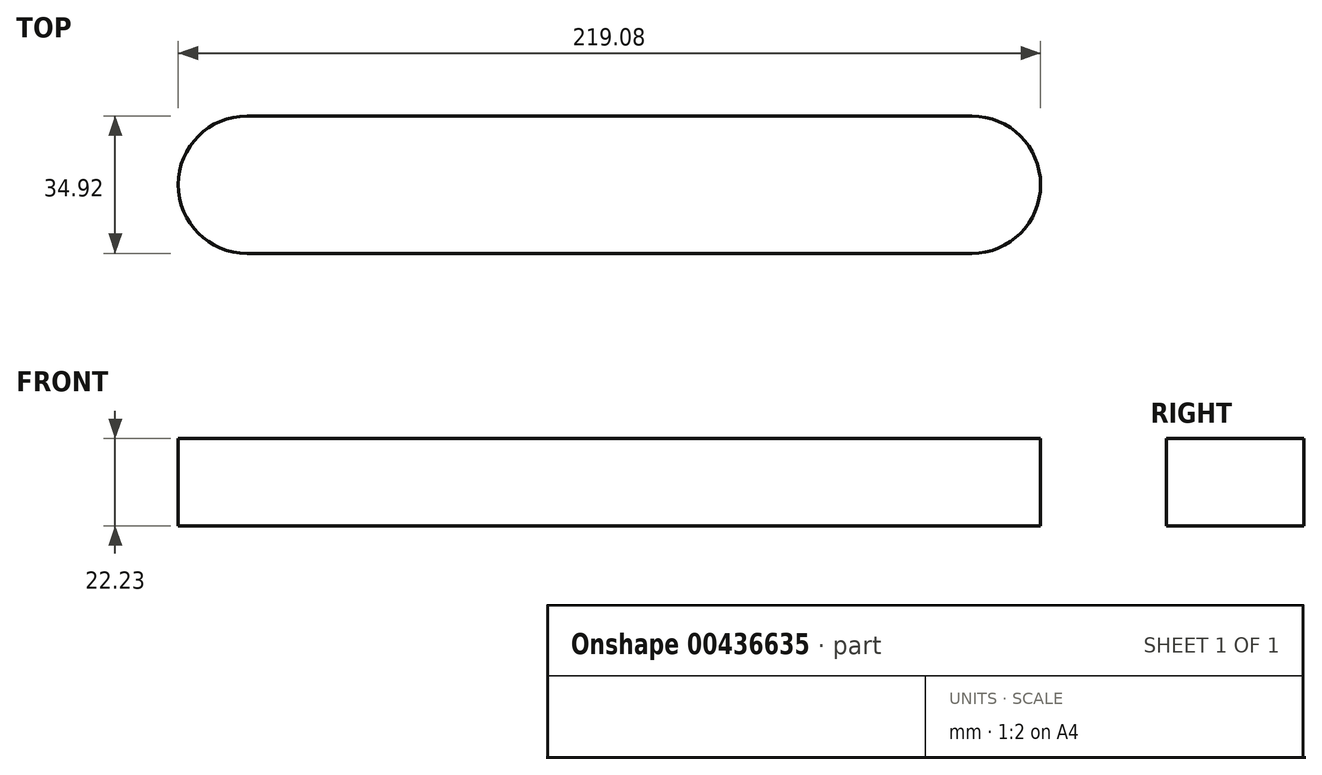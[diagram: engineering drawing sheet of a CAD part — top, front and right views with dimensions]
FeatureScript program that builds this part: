
annotation { "Feature Type Name" : "Feature", "Feature Type Description" : "" }
export const myFeature = defineFeature(function(context is Context, id is Id, definition is map)
    precondition{}
    {
        {
            var Q0;
            Q0=qCreatedBy(makeId("Top.planeOp"),FACE);
            var sketch = newSketch(context, id + "F0", { "sketchPlane" : qUnion([Q0])});
            skLineSegment(sketch, "E0", {"start": v(20.38, 40.27) * mm, "end": v(204.53, 40.27) * mm});
            skLineSegment(sketch, "E1", {"start": v(20.38, 5.35) * mm, "end": v(204.53, 5.35) * mm});
            skLineSegment(sketch, "E2", {"start": v(221.99, 22.8) * mm, "end": v(221.99, 22.8) * mm});
            skLineSegment(sketch, "E3", {"start": v(2.91, 22.8) * mm, "end": v(2.91, 22.8) * mm});
            skPoint(sketch, "E4.visualSharp", {"position": v(2.91, 40.27) * mm});
            skArc(sketch, "E4.filletArc", {"start": v(20.38, 40.27) * mm, "mid": v(8.03, 35.16) * mm, "end": v(2.91, 22.8) * mm});
            skPoint(sketch, "E5.visualSharp", {"position": v(2.91, 5.35) * mm});
            skArc(sketch, "E5.filletArc", {"start": v(2.91, 22.8) * mm, "mid": v(8.03, 10.46) * mm, "end": v(20.38, 5.35) * mm});
            skPoint(sketch, "E6.visualSharp", {"position": v(221.99, 5.35) * mm});
            skArc(sketch, "E6.filletArc", {"start": v(204.53, 5.35) * mm, "mid": v(216.87, 10.46) * mm, "end": v(221.99, 22.8) * mm});
            skPoint(sketch, "E7.visualSharp", {"position": v(221.99, 40.27) * mm});
            skArc(sketch, "E7.filletArc", {"start": v(221.99, 22.8) * mm, "mid": v(216.87, 35.16) * mm, "end": v(204.53, 40.27) * mm});
            skSolve(sketch);
        }
        {
            var Q0;
            Q0 = qSketchRegion(id + "F0", true);
            extrude(context, id + "F1", {"entities" : qUnion([Q0]), "depth" : 22.22 * mm, "offsetDistance" : 25.4 * mm});
        }
    });
